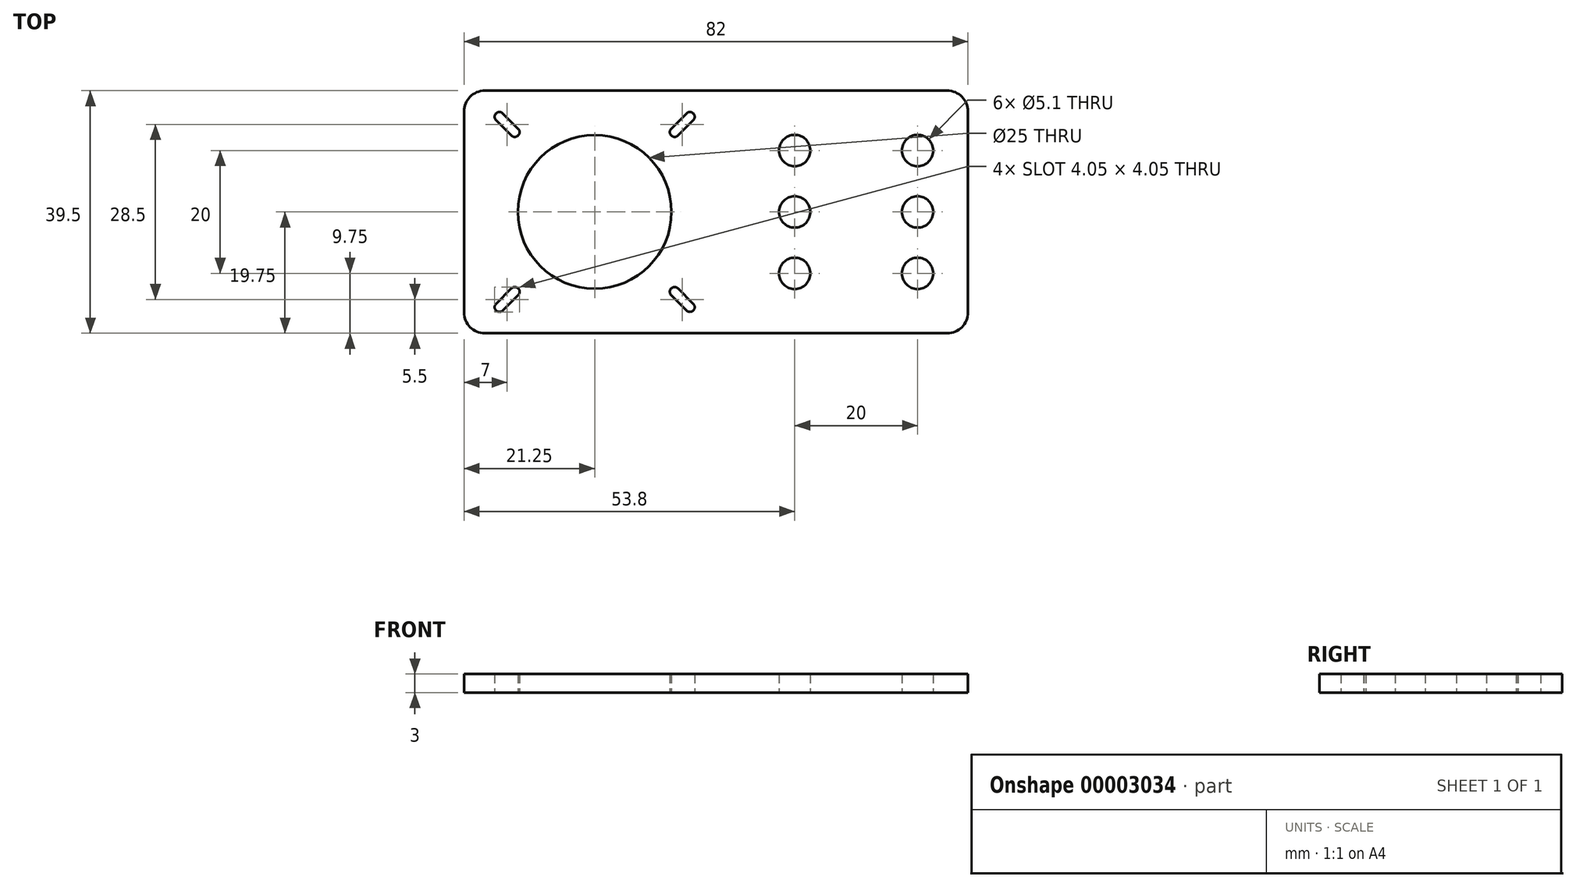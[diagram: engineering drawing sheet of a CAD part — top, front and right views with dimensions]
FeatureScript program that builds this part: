
annotation { "Feature Type Name" : "Feature", "Feature Type Description" : "" }
export const myFeature = defineFeature(function(context is Context, id is Id, definition is map)
    precondition{}
    {
        {
            var Q0;
            Q0=qCreatedBy(makeId("Top.planeOp"),FACE);
            var sketch = newSketch(context, id + "F0", { "sketchPlane" : qUnion([Q0])});
            skLineSegment(sketch, "E0.bottom", {"start": v(3.38, 0) * mm, "end": v(78.62, 0) * mm});
            skLineSegment(sketch, "E0.top", {"start": v(3.38, 39.5) * mm, "end": v(78.62, 39.5) * mm});
            skLineSegment(sketch, "E0.left", {"start": v(0, 3.38) * mm, "end": v(0, 36.12) * mm});
            skLineSegment(sketch, "E0.right", {"start": v(82, 3.38) * mm, "end": v(82, 36.12) * mm});
            skPoint(sketch, "E1.visualSharp", {"position": v(0, 39.5) * mm});
            skArc(sketch, "E1.filletArc", {"start": v(3.38, 39.5) * mm, "mid": v(0.99, 38.51) * mm, "end": v(0, 36.12) * mm});
            skPoint(sketch, "E2.visualSharp", {"position": v(0, 0) * mm});
            skArc(sketch, "E2.filletArc", {"start": v(0, 3.38) * mm, "mid": v(0.99, 0.99) * mm, "end": v(3.38, 0) * mm});
            skPoint(sketch, "E3.visualSharp", {"position": v(82, 39.5) * mm});
            skArc(sketch, "E3.filletArc", {"start": v(82, 36.12) * mm, "mid": v(81.01, 38.51) * mm, "end": v(78.62, 39.5) * mm});
            skPoint(sketch, "E4.visualSharp", {"position": v(82, 0) * mm});
            skArc(sketch, "E4.filletArc", {"start": v(78.62, 0) * mm, "mid": v(81.01, 0.99) * mm, "end": v(82, 3.38) * mm});
            skCircle(sketch, "E5", {"center": v(21.25, 19.75) * mm, "radius": 12.5 * mm});
            skArc(sketch, "E6", {"start": v(6.3, 35.8) * mm, "mid": v(5.2, 35.8) * mm, "end": v(5.2, 34.7) * mm});
            skArc(sketch, "E7", {"start": v(7.7, 32.2) * mm, "mid": v(8.8, 32.2) * mm, "end": v(8.8, 33.3) * mm});
            skLineSegment(sketch, "E8", {"start": v(5.2, 34.7) * mm, "end": v(7.7, 32.2) * mm});
            skLineSegment(sketch, "E9", {"start": v(6.3, 35.8) * mm, "end": v(8.8, 33.3) * mm});
            skLineSegment(sketch, "E10", {"start": v(21.25, 19.75) * mm, "end": v(8.75, 19.75) * mm, "construction": true});
            skLineSegment(sketch, "E11", {"start": v(21.25, 19.75) * mm, "end": v(21.25, 32.25) * mm, "construction": true});
            skLineSegment(sketch, "E12.0.MirrorCS", {"start": v(6.3, 3.7) * mm, "end": v(8.8, 6.2) * mm});
            skArc(sketch, "E13.0.MirrorCS", {"start": v(7.7, 7.3) * mm, "mid": v(8.8, 7.3) * mm, "end": v(8.8, 6.2) * mm});
            skLineSegment(sketch, "E14.0.MirrorCS", {"start": v(5.2, 4.8) * mm, "end": v(7.7, 7.3) * mm});
            skArc(sketch, "E15.0.MirrorCS", {"start": v(6.3, 3.7) * mm, "mid": v(5.2, 3.7) * mm, "end": v(5.2, 4.8) * mm});
            skLineSegment(sketch, "E16.0.MirrorCS", {"start": v(36.2, 35.8) * mm, "end": v(33.7, 33.3) * mm});
            skArc(sketch, "E17.0.MirrorCS", {"start": v(34.8, 32.2) * mm, "mid": v(33.7, 32.2) * mm, "end": v(33.7, 33.3) * mm});
            skLineSegment(sketch, "E18.0.MirrorCS", {"start": v(37.3, 34.7) * mm, "end": v(34.8, 32.2) * mm});
            skArc(sketch, "E19.0.MirrorCS", {"start": v(36.2, 35.8) * mm, "mid": v(37.3, 35.8) * mm, "end": v(37.3, 34.7) * mm});
            skLineSegment(sketch, "E20.0.MirrorCS", {"start": v(37.3, 4.8) * mm, "end": v(34.8, 7.3) * mm});
            skArc(sketch, "E21.0.MirrorCS", {"start": v(36.2, 3.7) * mm, "mid": v(37.3, 3.7) * mm, "end": v(37.3, 4.8) * mm});
            skLineSegment(sketch, "E22.0.MirrorCS", {"start": v(36.2, 3.7) * mm, "end": v(33.7, 6.2) * mm});
            skArc(sketch, "E23.0.MirrorCS", {"start": v(34.8, 7.3) * mm, "mid": v(33.7, 7.3) * mm, "end": v(33.7, 6.2) * mm});
            skCircle(sketch, "E24", {"center": v(53.8, 29.75) * mm, "radius": 2.55 * mm});
            skCircle(sketch, "E25", {"center": v(73.8, 29.75) * mm, "radius": 2.55 * mm});
            skCircle(sketch, "E26.0.MirrorC", {"center": v(53.8, 9.75) * mm, "radius": 2.55 * mm});
            skCircle(sketch, "E27.0.MirrorC", {"center": v(73.8, 9.75) * mm, "radius": 2.55 * mm});
            skCircle(sketch, "E28", {"center": v(53.8, 19.75) * mm, "radius": 2.55 * mm});
            skCircle(sketch, "E29", {"center": v(73.8, 19.75) * mm, "radius": 2.55 * mm});
            skSolve(sketch);
        }
        {
            var Q0;
            Q0=makeQuery(id+"F0.imprint","IMPRINT",FACE,{"disambiguationData":[TD([[makeQuery(id+"F0.imprint","IMPRINT",EDGE,{"derivedFrom":sQuery(id+"F0.wireOp",EDGE,"E0.bottom")}),1.0]])]});
            extrude(context, id + "F1", {"entities" : qUnion([Q0]), "depth" : 3 * mm});
        }
    });
